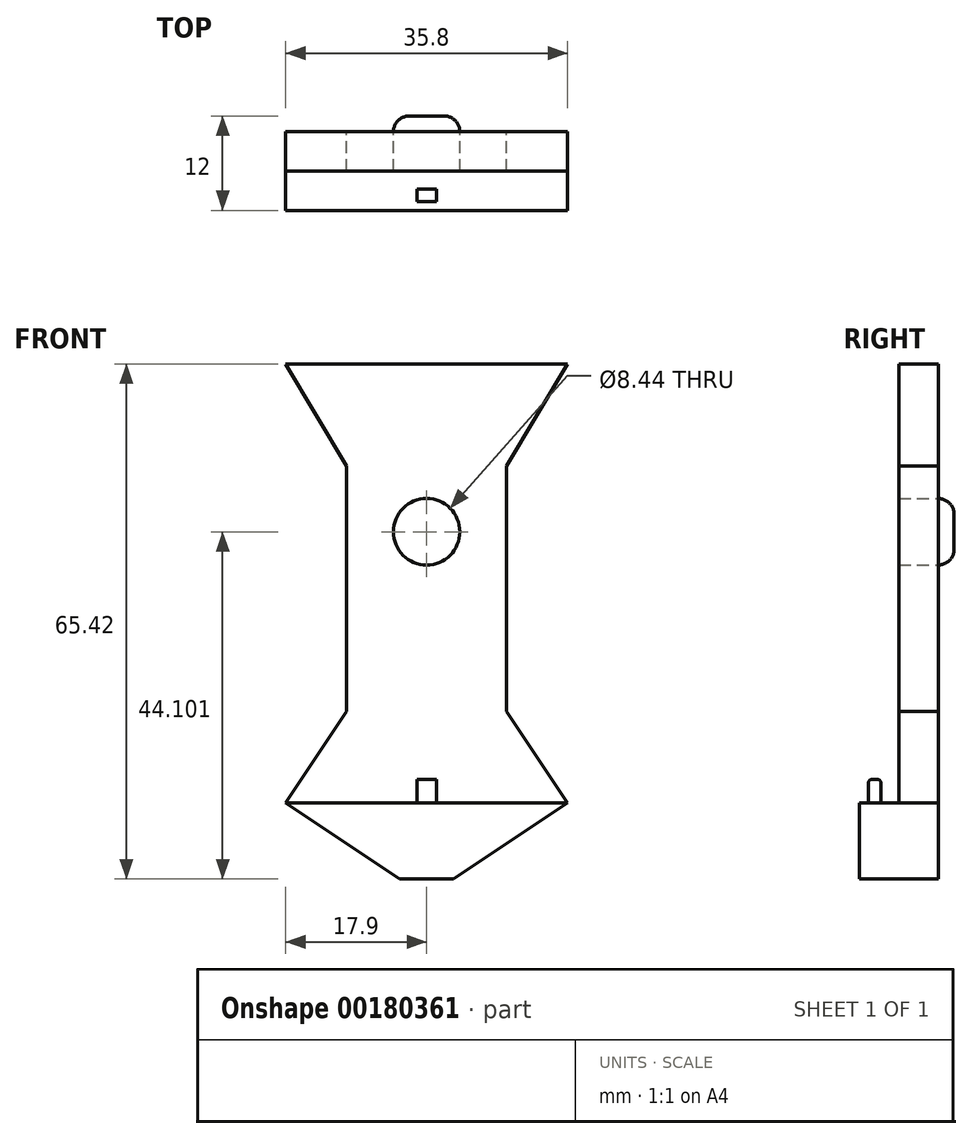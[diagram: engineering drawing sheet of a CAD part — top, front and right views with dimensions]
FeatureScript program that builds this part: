
annotation { "Feature Type Name" : "Feature", "Feature Type Description" : "" }
export const myFeature = defineFeature(function(context is Context, id is Id, definition is map)
    precondition{}
    {
        {
            var Q0;
            Q0=qCreatedBy(makeId("Front.planeOp"),FACE);
            var sketch = newSketch(context, id + "F0", { "sketchPlane" : qUnion([Q0])});
            skLineSegment(sketch, "E0.bottom", {"start": v(17.9, -32.71) * mm, "end": v(-17.9, -32.71) * mm});
            skLineSegment(sketch, "E0.top", {"start": v(17.9, 32.71) * mm, "end": v(-17.9, 32.71) * mm});
            skLineSegment(sketch, "E0.left", {"start": v(17.9, -32.71) * mm, "end": v(17.9, 32.71) * mm});
            skLineSegment(sketch, "E0.right", {"start": v(-17.9, -32.71) * mm, "end": v(-17.9, 32.71) * mm});
            skPoint(sketch, "E0.middle", {"position": v(0, 0) * mm});
            skLineSegment(sketch, "E1.bottom", {"start": v(-17.9, -32.71) * mm, "end": v(17.9, -32.71) * mm});
            skLineSegment(sketch, "E1.top", {"start": v(-17.9, -23.05) * mm, "end": v(17.9, -23.05) * mm});
            skLineSegment(sketch, "E1.left", {"start": v(-17.9, -32.71) * mm, "end": v(-17.9, -23.05) * mm});
            skLineSegment(sketch, "E1.right", {"start": v(17.9, -32.71) * mm, "end": v(17.9, -23.05) * mm});
            skPoint(sketch, "E1.middle", {"position": v(0, -27.88) * mm});
            skPoint(sketch, "E1.middle.positionSnap0", {"position": v(0, -32.71) * mm});
            skPoint(sketch, "E1.centerSnap0", {"position": v(0, -32.71) * mm});
            skCircle(sketch, "E2", {"center": v(0, 11.4) * mm, "radius": 4.22 * mm});
            skLineSegment(sketch, "E3", {"start": v(17.9, -23.05) * mm, "end": v(10.15, -11.43) * mm});
            skLineSegment(sketch, "E4", {"start": v(10.15, -11.43) * mm, "end": v(10.15, 19.71) * mm});
            skLineSegment(sketch, "E5", {"start": v(10.15, 19.71) * mm, "end": v(17.9, 32.71) * mm});
            skLineSegment(sketch, "E6.MirrorCS", {"start": v(-10.15, -11.43) * mm, "end": v(-10.15, 19.71) * mm});
            skLineSegment(sketch, "E7.MirrorCS", {"start": v(-17.9, -23.05) * mm, "end": v(-10.15, -11.43) * mm});
            skLineSegment(sketch, "E8.MirrorCS", {"start": v(-10.15, 19.71) * mm, "end": v(-17.9, 32.71) * mm});
            skLineSegment(sketch, "E9", {"start": v(-17.9, -23.05) * mm, "end": v(-3.42, -32.71) * mm});
            skLineSegment(sketch, "E10", {"start": v(17.9, -23.05) * mm, "end": v(3.42, -32.71) * mm});
            skSolve(sketch);
        }
        {
            var Q0;
            Q0=makeQuery(id+"F0.imprint","IMPRINT",FACE,{"disambiguationData":[TD([[makeQuery(id+"F0.imprint","IMPRINT",EDGE,{"derivedFrom":sQuery(id+"F0.wireOp",EDGE,"E0.top")}),1.0]])]});
            extrude(context, id + "F1", {"entities" : qUnion([Q0]), "depth" : 5 * mm});
        }
        {
            var Q0;
            Q0=makeQuery(id+"F0.imprint","IMPRINT",FACE,{"disambiguationData":[TD([[makeQuery(id+"F0.imprint","IMPRINT",EDGE,{"derivedFrom":sQuery(id+"F0.wireOp",EDGE,"E1.top")}),-1.0]])]});
            extrude(context, id + "F2", {"entities" : qUnion([Q0]), "operationType" : NewBodyOperationType.ADD, "depth" : 10 * mm});
        }
        {
            var Q0;
            Q0=makeQuery(id+"F0.imprint","IMPRINT",FACE,{"disambiguationData":[TD([[makeQuery(id+"F0.imprint","IMPRINT",EDGE,{"derivedFrom":sQuery(id+"F0.wireOp",EDGE,"E2")}),1.0]])]});
            var Q1;
            Q1=sQuery(id+"F0.wireOp",EDGE,"E2");
            extrude(context, id + "F3", {"entities" : qUnion([Q0]), "surfaceEntities" : qUnion([Q1]), "oppositeDirection" : true, "depth" : 2 * mm});
        }
        {
            var Q0;
            Q0=makeQuery(id+"F3.opExtrude","CAP_EDGE",EDGE,{"disambiguationData":[OSD([sQuery(id+"F0.wireOp",EDGE,"E2")])],"isStart":false});
            fillet(context, id + "F4", {"entities" : qUnion([Q0]), "radius" : 2 * mm, "allowEdgeOverflow" : false});
        }
        {
            var Q0;
            Q0=makeQuery(id+"F0.imprint","IMPRINT",FACE,{"disambiguationData":[TD([[makeQuery(id+"F0.imprint","IMPRINT",EDGE,{"derivedFrom":sQuery(id+"F0.wireOp",EDGE,"E2")}),1.0]])]});
            var Q1;
            Q1=sQuery(id+"F0.wireOp",EDGE,"E2");
            extrude(context, id + "F5", {"entities" : qUnion([Q0]), "surfaceEntities" : qUnion([Q1]), "depth" : 5 * mm});
        }
        {
            var Q0;
            Q0=makeQuery(id+"F2.opExtrude","SWEPT_FACE",FACE,{"disambiguationData":[OSD([sQuery(id+"F0.wireOp",EDGE,"E1.top")])]});
            var sketch = newSketch(context, id + "F6", { "sketchPlane" : qUnion([Q0])});
            skLineSegment(sketch, "E11.bottom", {"start": v(1.25, -8.87) * mm, "end": v(-1.25, -8.87) * mm});
            skLineSegment(sketch, "E11.top", {"start": v(1.25, -7.29) * mm, "end": v(-1.25, -7.29) * mm});
            skLineSegment(sketch, "E11.left", {"start": v(1.25, -8.87) * mm, "end": v(1.25, -7.29) * mm});
            skLineSegment(sketch, "E11.right", {"start": v(-1.25, -8.87) * mm, "end": v(-1.25, -7.29) * mm});
            skPoint(sketch, "E11.middle", {"position": v(0, -8.08) * mm});
            skSolve(sketch);
        }
        {
            var Q0;
            Q0 = qSketchRegion(id + "F6", true);
            extrude(context, id + "F7", {"entities" : qUnion([Q0]), "operationType" : NewBodyOperationType.ADD, "depth" : 3 * mm});
        }
        {
            var Q0;
            Q0=makeQuery(id+"F7.opExtrude","CAP_EDGE",EDGE,{"disambiguationData":[OSD([sQuery(id+"F6.wireOp",EDGE,"E11.bottom")])],"isStart":false});
            var Q1;
            Q1=makeQuery(id+"F7.opExtrude","CAP_EDGE",EDGE,{"disambiguationData":[OSD([sQuery(id+"F6.wireOp",EDGE,"E11.top")])],"isStart":false});
            fillet(context, id + "F8", {"entities" : qUnion([Q0, Q1]), "radius" : .5 * mm, "tangentPropagation" : true, "allowEdgeOverflow" : false});
        }
    });
